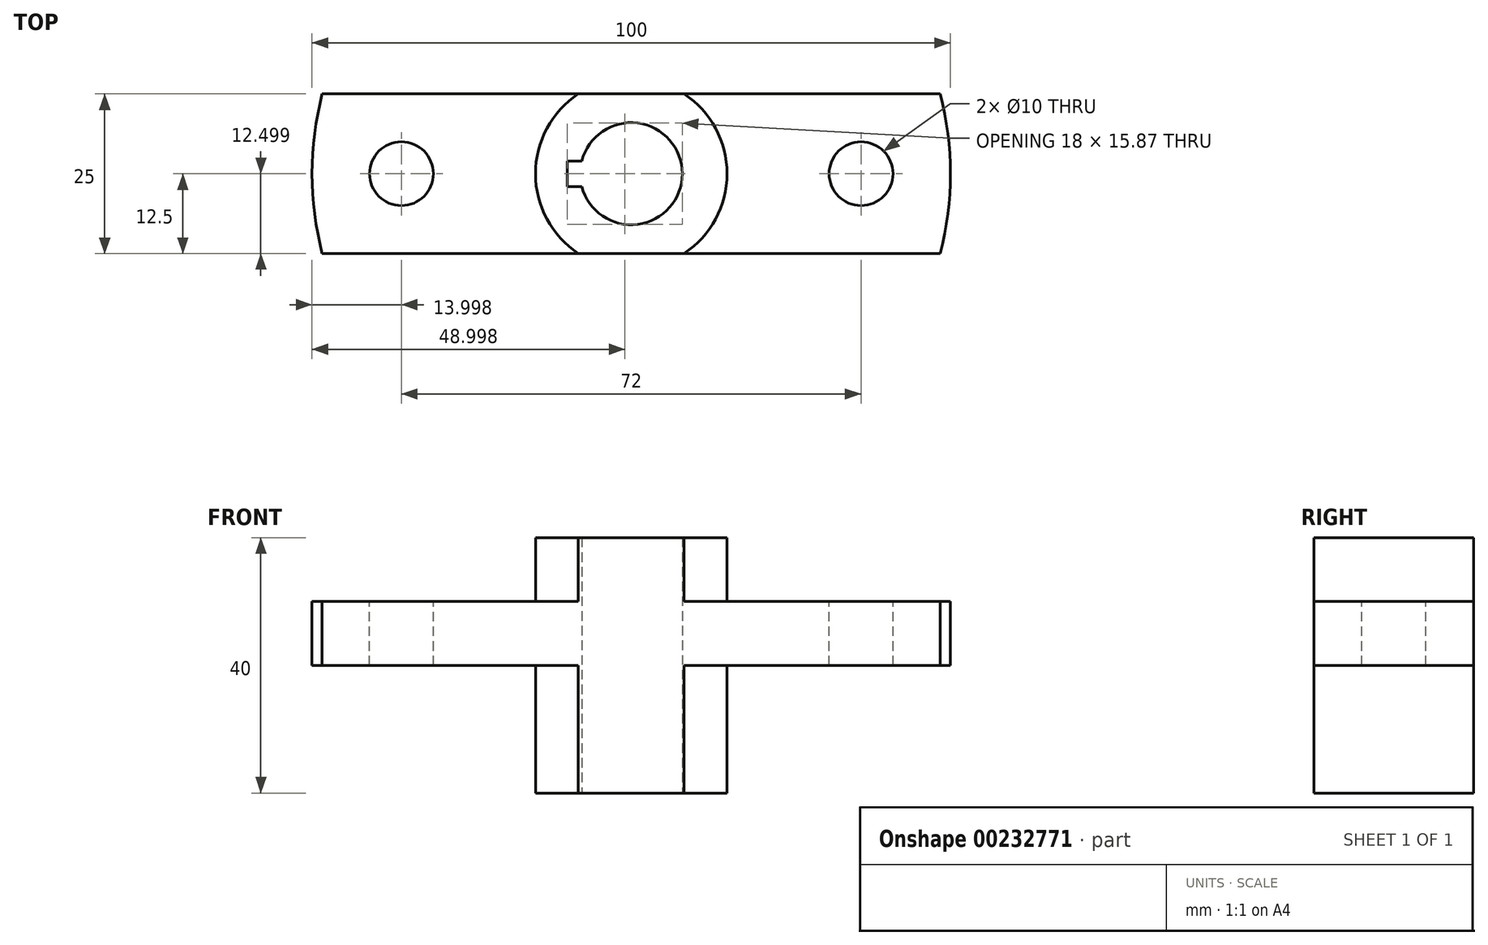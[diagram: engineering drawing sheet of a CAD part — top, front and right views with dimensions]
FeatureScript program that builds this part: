
annotation { "Feature Type Name" : "Feature", "Feature Type Description" : "" }
export const myFeature = defineFeature(function(context is Context, id is Id, definition is map)
    precondition{}
    {
        {
            var Q0;
            Q0=qCreatedBy(makeId("Top.planeOp"),FACE);
            var sketch = newSketch(context, id + "F0", { "sketchPlane" : qUnion([Q0])});
            skLineSegment(sketch, "E0", {"start": v(-60.27, 18.36) * mm, "end": v(39.73, 18.36) * mm, "construction": true});
            skLineSegment(sketch, "E1", {"start": v(-10.27, 30.86) * mm, "end": v(-10.27, 5.86) * mm, "construction": true});
            skPoint(sketch, "E2", {"position": v(-10.27, 18.36) * mm});
            skArc(sketch, "E3", {"start": v(-58.68, 30.86) * mm, "mid": v(-60.27, 18.36) * mm, "end": v(-58.68, 5.86) * mm});
            skArc(sketch, "E4", {"start": v(-18.02, 16.36) * mm, "mid": v(-2.27, 18.36) * mm, "end": v(-18.02, 20.36) * mm});
            skLineSegment(sketch, "E5.0", {"start": v(-58.68, 5.86) * mm, "end": v(38.14, 5.86) * mm});
            skLineSegment(sketch, "E6.0", {"start": v(-58.68, 30.86) * mm, "end": v(38.14, 30.86) * mm});
            skLineSegment(sketch, "E7.0", {"start": v(-20.27, 20.36) * mm, "end": v(-20.27, 16.36) * mm});
            skLineSegment(sketch, "E8", {"start": v(-20.27, 20.36) * mm, "end": v(-18.02, 20.36) * mm});
            skLineSegment(sketch, "E9.MirrorCS", {"start": v(-20.27, 16.36) * mm, "end": v(-18.02, 16.36) * mm});
            skArc(sketch, "E10.trimOffspring", {"start": v(38.14, 5.86) * mm, "mid": v(39.73, 18.36) * mm, "end": v(38.14, 30.86) * mm});
            skCircle(sketch, "E11", {"center": v(-46.27, 18.36) * mm, "radius": 5 * mm});
            skCircle(sketch, "E12.MirrorC", {"center": v(25.73, 18.36) * mm, "radius": 5 * mm});
            skArc(sketch, "E13", {"start": v(-18.56, 30.86) * mm, "mid": v(-25.27, 18.36) * mm, "end": v(-18.56, 5.86) * mm});
            skArc(sketch, "E14.trimOffspring", {"start": v(-1.98, 5.86) * mm, "mid": v(4.73, 18.36) * mm, "end": v(-1.98, 30.86) * mm});
            skSolve(sketch);
        }
        {
            var Q0;
            Q0=makeQuery(id+"F0.imprint","IMPRINT",FACE,{"disambiguationData":[TD([[makeQuery(id+"F0.imprint","IMPRINT",EDGE,{"derivedFrom":sQuery(id+"F0.wireOp",EDGE,"E4")}),-1.0]])]});
            extrude(context, id + "F1", {"entities" : qUnion([Q0]), "depth" : 10 * mm, "hasSecondDirection" : true, "secondDirectionOppositeDirection" : true, "secondDirectionDepth" : 30 * mm});
        }
        {
            var Q0;
            {var subQ1=sQuery(id+"F0.wireOp",EDGE,"E3");Q0=makeQuery(id+"F0.imprint","IMPRINT",FACE,{"disambiguationData":[TD([[makeQuery(id+"F0.imprint","IMPRINT",EDGE,{"derivedFrom":subQ1}),1.0]])]});}
            var Q1;
            {var subQ0=sQuery(id+"F0.wireOp",EDGE,"E10.trimOffspring");Q1=makeQuery(id+"F0.imprint","IMPRINT",FACE,{"disambiguationData":[TD([[makeQuery(id+"F0.imprint","IMPRINT",EDGE,{"derivedFrom":subQ0}),1.0]])]});}
            extrude(context, id + "F2", {"entities" : qUnion([Q0, Q1]), "operationType" : NewBodyOperationType.ADD, "oppositeDirection" : true, "depth" : 10 * mm});
        }
    });
